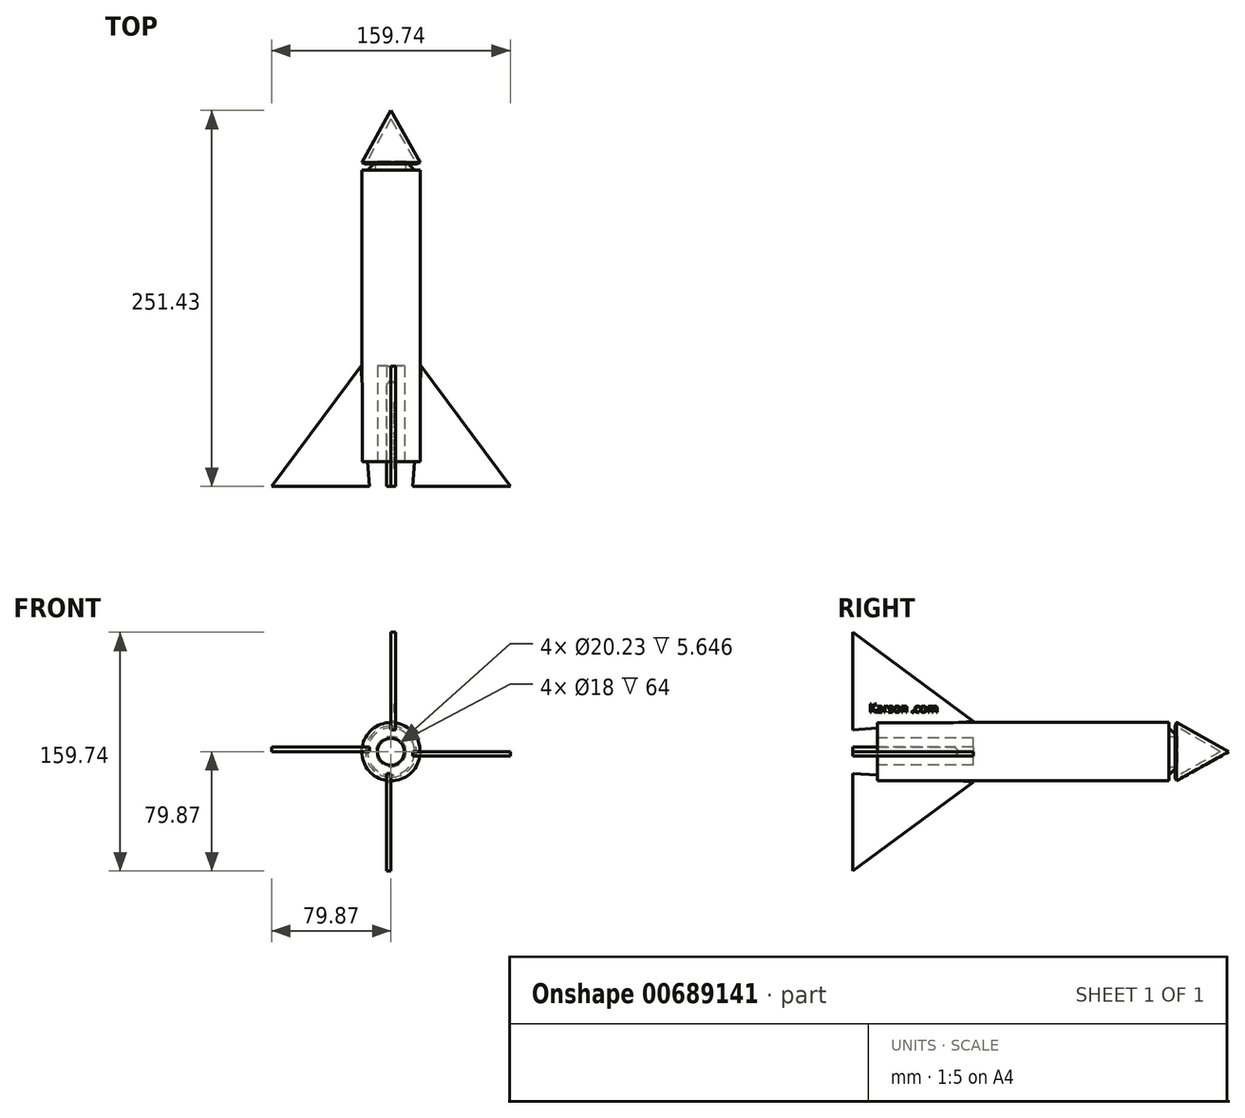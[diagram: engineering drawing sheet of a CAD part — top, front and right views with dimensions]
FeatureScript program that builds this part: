
annotation { "Feature Type Name" : "Feature", "Feature Type Description" : "" }
export const myFeature = defineFeature(function(context is Context, id is Id, definition is map)
    precondition{}
    {
        {
            var Q0;
            Q0=qCreatedBy(makeId("Top.planeOp"),FACE);
            var sketch = newSketch(context, id + "F0", { "sketchPlane" : qUnion([Q0])});
            skLineSegment(sketch, "E0", {"start": v(0, 111.98) * mm, "end": v(0, -122.83) * mm});
            skLineSegment(sketch, "E1", {"start": v(0, -122.83) * mm, "end": v(19.53, -122.83) * mm});
            skLineSegment(sketch, "E2", {"start": v(19.53, -122.83) * mm, "end": v(19.53, 71.97) * mm});
            skLineSegment(sketch, "E3", {"start": v(19.53, 71.97) * mm, "end": v(15.76, 71.97) * mm});
            skLineSegment(sketch, "E4", {"start": v(21.4, 77.62) * mm, "end": v(15.76, 77.62) * mm});
            skLineSegment(sketch, "E5", {"start": v(10.12, 71.97) * mm, "end": v(0, 71.97) * mm});
            skLineSegment(sketch, "E6", {"start": v(10.12, 77.62) * mm, "end": v(10.12, 71.97) * mm});
            skLineSegment(sketch, "E7", {"start": v(10.12, 71.97) * mm, "end": v(10.12, 77.62) * mm});
            skLineSegment(sketch, "E8", {"start": v(16.32, 77.62) * mm, "end": v(21.4, 77.62) * mm});
            skPoint(sketch, "E9.orphan", {"position": v(5.88, 77.62) * mm});
            skLineSegment(sketch, "E10", {"start": v(19.53, 76.99) * mm, "end": v(0, 111.98) * mm});
            skLineSegment(sketch, "E11", {"start": v(0, 106.32) * mm, "end": v(17.13, 76.18) * mm});
            skLineSegment(sketch, "E12", {"start": v(19.53, 76.99) * mm, "end": v(17.13, 76.18) * mm});
            skPoint(sketch, "E13.end.orphan", {"position": v(22.82, 71.97) * mm});
            skLineSegment(sketch, "E14", {"start": v(10.12, 77.62) * mm, "end": v(15.76, 71.97) * mm});
            skSolve(sketch);
        }
        {
            var Q0;
            Q0 = qSketchRegion(id + "F0", true);
            var Q1;
            Q1=sQuery(id+"F0.wireOp",EDGE,"E0");
            revolve(context, id + "F1", {"entities" : qUnion([Q0]), "axis" : qUnion([Q1]), "revolveType" : RevolveType.FULL});
        }
        {
            var Q0;
            Q0=qCreatedBy(makeId("Top.planeOp"),FACE);
            var sketch = newSketch(context, id + "F2", { "sketchPlane" : qUnion([Q0])});
            skLineSegment(sketch, "E15", {"start": v(-20.22, -58.97) * mm, "end": v(-79.87, -139.45) * mm});
            skLineSegment(sketch, "E16", {"start": v(-79.87, -139.45) * mm, "end": v(-14.5, -139.45) * mm});
            skLineSegment(sketch, "E17", {"start": v(-20.22, -58.97) * mm, "end": v(-14.5, -139.45) * mm});
            skSolve(sketch);
        }
        {
            var Q0;
            Q0=makeQuery(id+"F2.imprint","IMPRINT",FACE,{"disambiguationData":[TD([[makeQuery(id+"F2.imprint","IMPRINT",EDGE,{"derivedFrom":sQuery(id+"F2.wireOp",EDGE,"E15")}),1.0]])]});
            extrude(context, id + "F3", {"entities" : qUnion([Q0]), "operationType" : NewBodyOperationType.ADD, "depth" : 3 * mm, "offsetDistance" : 25 * mm});
        }
        {
            var Q0;
            Q0=makeQuery(id+"F1.opRevolve","SWEPT_BODY",BODY,{"disambiguationData":[OSD([sQuery(id+"F0.wireOp",EDGE,"E0"),sQuery(id+"F0.wireOp",EDGE,"E1"),sQuery(id+"F0.wireOp",EDGE,"E2"),sQuery(id+"F0.wireOp",EDGE,"E3"),sQuery(id+"F0.wireOp",EDGE,"Rc6vJgzp-w8tF-kgaV-ZqLD-aZW04c6TfQp7"),sQuery(id+"F0.wireOp",EDGE,"E4"),sQuery(id+"F0.wireOp",EDGE,"E13"),sQuery(id+"F0.wireOp",EDGE,"E5")])]});
            var Q1;
            Q1=makeQuery(id+"F1.opRevolve","SWEPT_FACE",FACE,{"disambiguationData":[OSD([sQuery(id+"F0.wireOp",EDGE,"E2")])]});
            circularPattern(context, id + "F4", {"entities" : qUnion([Q0]), "axis" : qUnion([Q1]), "angle" : 360 * degree, "instanceCount" : 4, "equalSpace" : true});
        }
        {
            var Q0;
            Q0=makeQuery(id+"F1.opRevolve","SWEPT_FACE",FACE,{"disambiguationData":[OSD([sQuery(id+"F0.wireOp",EDGE,"E1")])]});
            var sketch = newSketch(context, id + "F5", { "sketchPlane" : qUnion([Q0])});
            skCircle(sketch, "E18", {"center": v(0, 0) * mm, "radius": 9 * mm});
            skSolve(sketch);
        }
        {
            var Q0;
            Q0 = qSketchRegion(id + "F5", true);
            extrude(context, id + "F6", {"entities" : qUnion([Q0]), "operationType" : NewBodyOperationType.REMOVE, "oppositeDirection" : true, "depth" : 64 * mm, "offsetDistance" : 25 * mm});
        }
        {
            var Q0;
            Q0=makeQuery(id+"F4.opPattern","COPY",FACE,{"derivedFrom":makeQuery(id+"F3.opExtrude","CAP_FACE",FACE,{"disambiguationData":[OSD([sQuery(id+"F2.wireOp",EDGE,"E15"),sQuery(id+"F2.wireOp",EDGE,"E16"),sQuery(id+"F2.wireOp",EDGE,"E17")])],"isStart":false}),"instanceName":"1"});
            var sketch = newSketch(context, id + "F7", { "sketchPlane" : qUnion([Q0])});
            skText(sketch, "E19", { "text": "Karson .com", "fontName": "OpenSans-Regular.ttf"});
            const initialGuessF7  = {"E19": [-0.1285, 0.02623, 1, 0, 0.00571]};
            skSetInitialGuess(sketch, initialGuessF7);
            skSolve(sketch);
        }
        {
            var Q0;
            Q0 = qSketchRegion(id + "F7", true);
            extrude(context, id + "F8", {"entities" : qUnion([Q0]), "operationType" : NewBodyOperationType.REMOVE, "oppositeDirection" : true, "depth" : 1 * mm, "offsetDistance" : 25 * mm});
        }
    });
